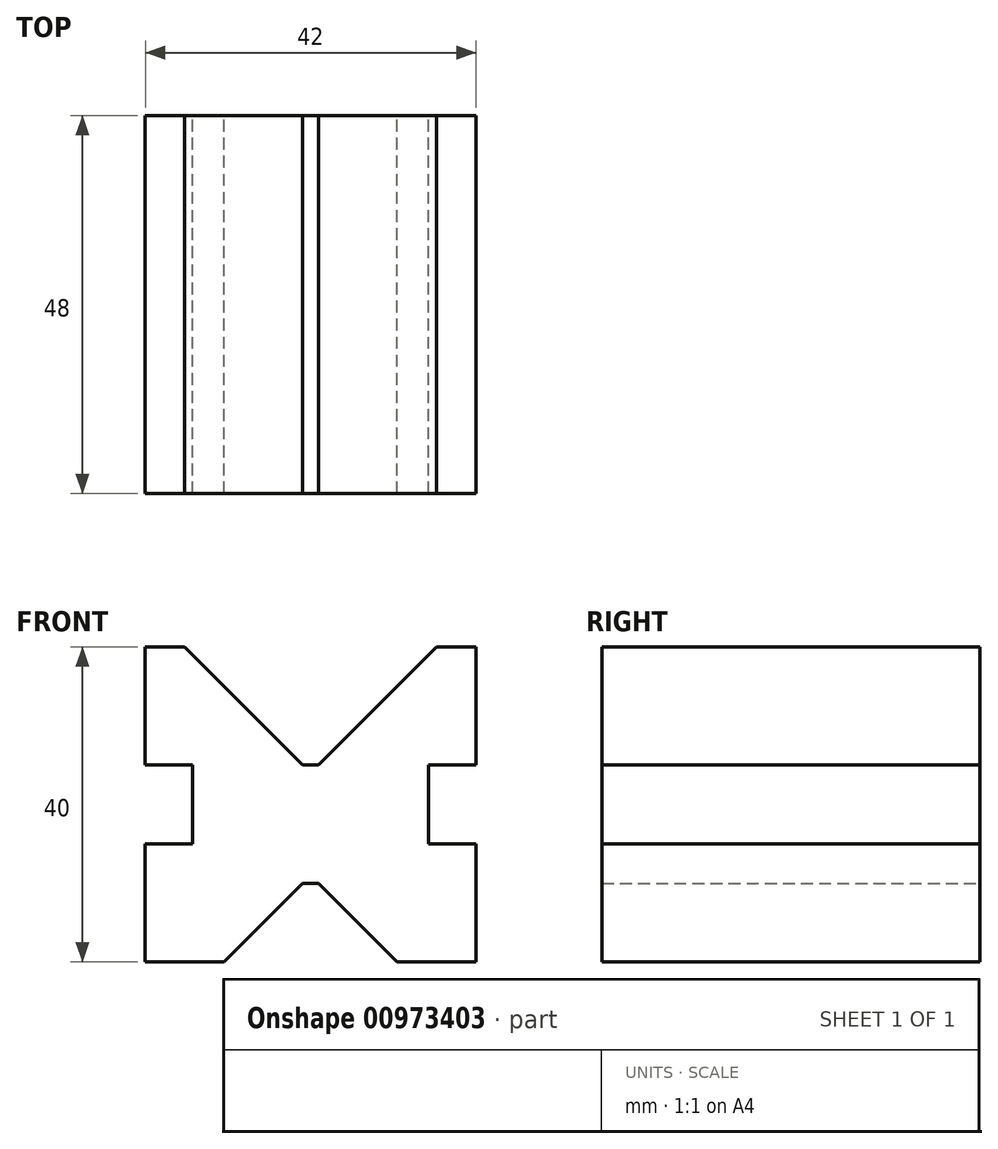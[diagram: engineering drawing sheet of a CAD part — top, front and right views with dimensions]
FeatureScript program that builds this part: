
annotation { "Feature Type Name" : "Feature", "Feature Type Description" : "" }
export const myFeature = defineFeature(function(context is Context, id is Id, definition is map)
    precondition{}
    {
        {
            var Q0;
            Q0=qCreatedBy(makeId("Front.planeOp"),FACE);
            var sketch = newSketch(context, id + "F0", { "sketchPlane" : qUnion([Q0])});
            skLineSegment(sketch, "E0.bottom", {"start": v(-16.54, -6.43) * mm, "end": v(-6.54, -6.43) * mm});
            skLineSegment(sketch, "E0.top", {"start": v(-16.54, 33.57) * mm, "end": v(-11.54, 33.57) * mm});
            skLineSegment(sketch, "E0.left", {"start": v(-16.54, -6.43) * mm, "end": v(-16.54, 8.57) * mm});
            skLineSegment(sketch, "E1", {"start": v(-16.54, 33.57) * mm, "end": v(-16.54, 18.57) * mm});
            skLineSegment(sketch, "E2", {"start": v(-16.54, 18.57) * mm, "end": v(-10.54, 18.57) * mm});
            skLineSegment(sketch, "E3", {"start": v(-16.54, 8.57) * mm, "end": v(-10.54, 8.57) * mm});
            skLineSegment(sketch, "E4", {"start": v(-10.54, 18.57) * mm, "end": v(-10.54, 8.57) * mm});
            skLineSegment(sketch, "E5.trimOffspring", {"start": v(-16.54, 18.57) * mm, "end": v(-16.54, 33.57) * mm});
            skLineSegment(sketch, "E6", {"start": v(-11.54, 33.57) * mm, "end": v(3.46, 18.57) * mm});
            skLineSegment(sketch, "E7", {"start": v(-6.54, -6.43) * mm, "end": v(3.46, 3.57) * mm});
            skPoint(sketch, "E8.orphan", {"position": v(3.46, -6.43) * mm});
            skLineSegment(sketch, "E9.bottom", {"start": v(3.46, 18.57) * mm, "end": v(4.46, 18.57) * mm});
            skLineSegment(sketch, "E9.top", {"start": v(3.46, 3.57) * mm, "end": v(4.46, 3.57) * mm});
            skLineSegment(sketch, "E9.right", {"start": v(4.46, 18.57) * mm, "end": v(4.46, 3.57) * mm});
            skSolve(sketch);
        }
        {
            var Q0;
            Q0=makeQuery(id+"F0.imprint","IMPRINT",FACE,{"disambiguationData":[TD([[makeQuery(id+"F0.imprint","IMPRINT",EDGE,{"derivedFrom":sQuery(id+"F0.wireOp",EDGE,"E0.top")}),-1.0]])]});
            extrude(context, id + "F1", {"entities" : qUnion([Q0]), "endBound" : BoundingType.SYMMETRIC, "depth" : 24 * mm, "offsetDistance" : 25 * mm});
        }
        {
            var Q0;
            Q0=makeQuery(id+"F1.opExtrude","SWEPT_BODY",BODY,{"disambiguationData":[OSD([sQuery(id+"F0.wireOp",EDGE,"E0.top"),sQuery(id+"F0.wireOp",EDGE,"E0.left"),sQuery(id+"F0.wireOp",EDGE,"E2"),sQuery(id+"F0.wireOp",EDGE,"E3"),sQuery(id+"F0.wireOp",EDGE,"E4"),sQuery(id+"F0.wireOp",EDGE,"E5.trimOffspring"),sQuery(id+"F0.wireOp",EDGE,"E0.bottom"),sQuery(id+"F0.wireOp",EDGE,"E6"),sQuery(id+"F0.wireOp",EDGE,"E7"),sQuery(id+"F0.wireOp",EDGE,"E9.bottom"),sQuery(id+"F0.wireOp",EDGE,"E9.top"),sQuery(id+"F0.wireOp",EDGE,"E9.right")])]});
            var Q1;
            Q1=makeQuery(id+"F1.opExtrude","CAP_FACE",FACE,{"disambiguationData":[OSD([sQuery(id+"F0.wireOp",EDGE,"E0.top"),sQuery(id+"F0.wireOp",EDGE,"E0.left"),sQuery(id+"F0.wireOp",EDGE,"E2"),sQuery(id+"F0.wireOp",EDGE,"E3"),sQuery(id+"F0.wireOp",EDGE,"E4"),sQuery(id+"F0.wireOp",EDGE,"E5.trimOffspring"),sQuery(id+"F0.wireOp",EDGE,"E0.bottom"),sQuery(id+"F0.wireOp",EDGE,"E6"),sQuery(id+"F0.wireOp",EDGE,"E7"),sQuery(id+"F0.wireOp",EDGE,"E9.bottom"),sQuery(id+"F0.wireOp",EDGE,"E9.top"),sQuery(id+"F0.wireOp",EDGE,"E9.right")])],"isStart":true});
            mirror(context, id + "F2", {"operationType" : NewBodyOperationType.ADD, "entities" : qUnion([Q0]), "mirrorPlane" : qUnion([Q1])});
        }
        {
            var Q0;
            Q0=makeQuery(id+"F1.opExtrude","SWEPT_BODY",BODY,{"disambiguationData":[OSD([sQuery(id+"F0.wireOp",EDGE,"E0.top"),sQuery(id+"F0.wireOp",EDGE,"E0.left"),sQuery(id+"F0.wireOp",EDGE,"E2"),sQuery(id+"F0.wireOp",EDGE,"E3"),sQuery(id+"F0.wireOp",EDGE,"E4"),sQuery(id+"F0.wireOp",EDGE,"E5.trimOffspring"),sQuery(id+"F0.wireOp",EDGE,"E0.bottom"),sQuery(id+"F0.wireOp",EDGE,"E6"),sQuery(id+"F0.wireOp",EDGE,"E7"),sQuery(id+"F0.wireOp",EDGE,"E9.bottom"),sQuery(id+"F0.wireOp",EDGE,"E9.top"),sQuery(id+"F0.wireOp",EDGE,"E9.right")])]});
            var Q1;
            {var subQ0=makeQuery(id+"F1.opExtrude","SWEPT_FACE",FACE,{"disambiguationData":[OSD([sQuery(id+"F0.wireOp",EDGE,"E9.right")])]});Q1=makeQuery(id+"F2.boolean.opBoolean","MERGE",FACE,{"derivedFrom":[subQ0,makeQuery(id+"F2.opPattern","COPY",FACE,{"derivedFrom":subQ0,"instanceName":"1"})]});}
            mirror(context, id + "F3", {"operationType" : NewBodyOperationType.ADD, "entities" : qUnion([Q0]), "mirrorPlane" : qUnion([Q1])});
        }
    });
